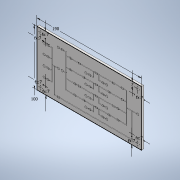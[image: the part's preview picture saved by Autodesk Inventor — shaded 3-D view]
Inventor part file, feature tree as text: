
AUTODESK INVENTOR PART (.ipt)
format: ipt  version: 2021 (Build 250183000, 183)  size: 751,104 bytes
history: native  units: in
note: dims shown in document units (in); Inventor stores cm internally (conversion verified against a paired STEP export)
features: other x9, extrude x4, hole x2, surface_op x1
ambient origin geometry x8: Origin, YZ Plane, XZ Plane, XY Plane, X Axis, Y Axis, Z Axis, Center Point
bodies: Solid1 (feature_tree)
feature tree (16):
  other  "points for corner holes"
  extrude  "Extrusion base plate"  Depth=6.6929in
  other  "plane above base plate to create rib"
  other  "channels and points for valves and for connectors"
  other  "channels as rib"
  extrude  "extrusion of rib to get cutout"  Depth=8.6614in
  other  "valve shape"
  extrude  "valve space extrusion"  Depth=0.1969in
  extrude  "valve bar extrusion"  Depth=0.3543in
  other  "all valve spaces"
  other  "projected point for every hole"
  hole  "holes for connectors"  [1 undecoded]
  hole  "holes in corners"  [1 undecoded]
  other  "valve bar shape"
  other  "Projected points for every valve"
  surface_op  "surface of rib as sketch"
note: 2 required parameter values undecoded (feature->parameter linkage not recoverable at this tier; creation-order binding heuristic only, values carry confidence <= 0.55)
